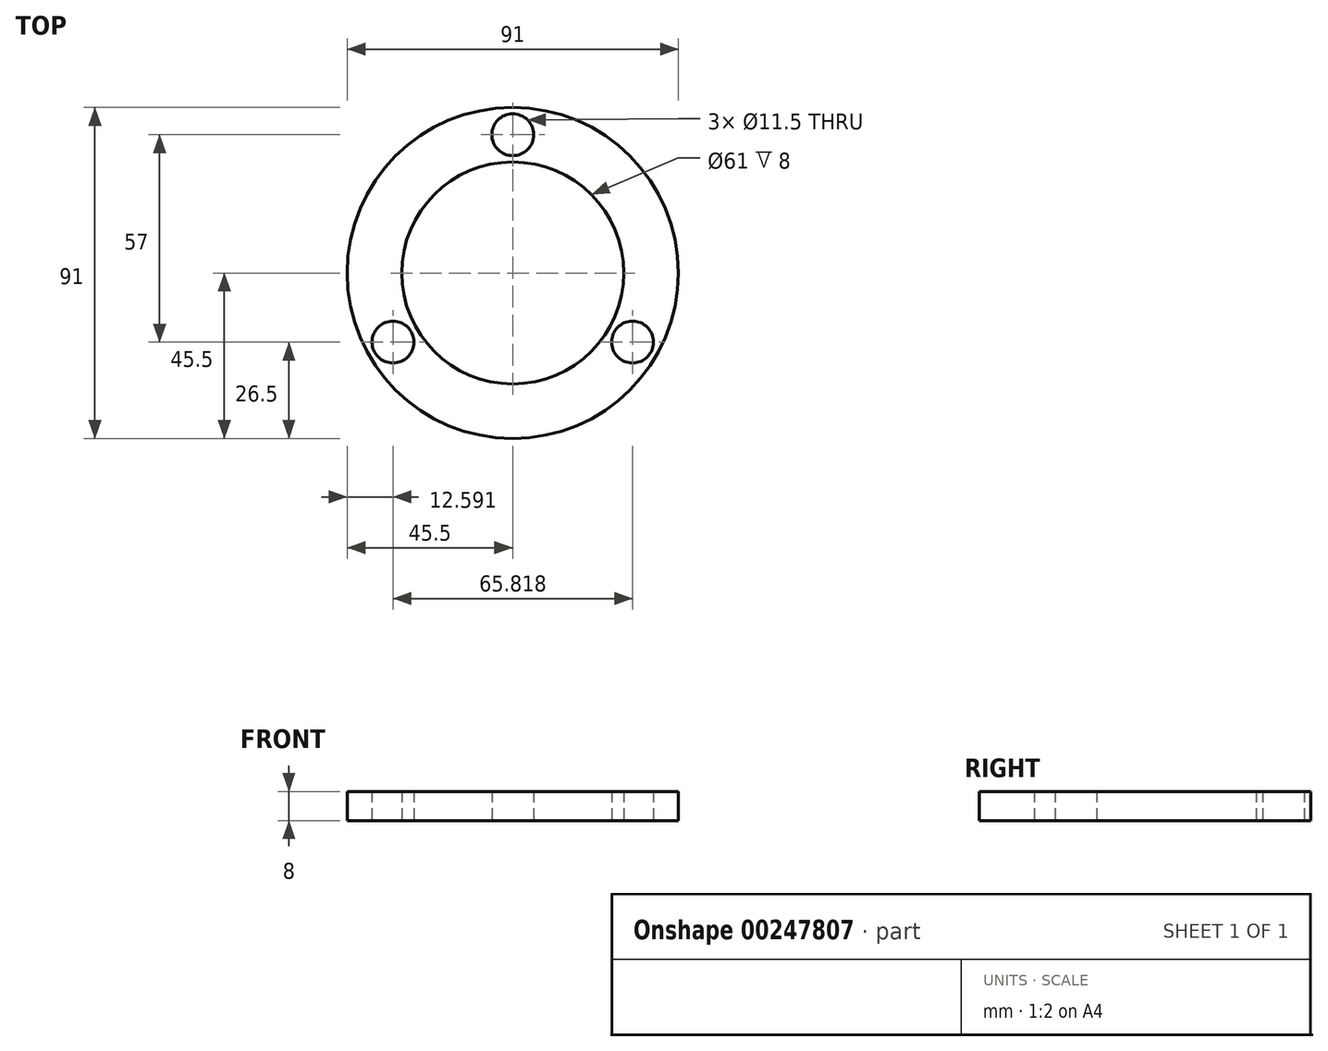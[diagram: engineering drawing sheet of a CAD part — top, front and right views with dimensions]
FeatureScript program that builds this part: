
annotation { "Feature Type Name" : "Feature", "Feature Type Description" : "" }
export const myFeature = defineFeature(function(context is Context, id is Id, definition is map)
    precondition{}
    {
        {
            var Q0;
            Q0=qCreatedBy(makeId("Top.planeOp"),FACE);
            var sketch = newSketch(context, id + "F0", { "sketchPlane" : qUnion([Q0])});
            skCircle(sketch, "E0", {"center": v(0, 0) * mm, "radius": 38 * mm});
            skCircle(sketch, "E1", {"center": v(0, 0) * mm, "radius": 45.5 * mm});
            skCircle(sketch, "E2", {"center": v(0, 0) * mm, "radius": 30.5 * mm});
            skCircle(sketch, "E3.cCircle", {"center": v(0, 0) * mm, "radius": 38 * mm, "construction": true});
            skLineSegment(sketch, "E3.0", {"start": v(0, 38) * mm, "end": v(32.9, -19) * mm});
            skLineSegment(sketch, "E3.1", {"start": v(32.9, -19) * mm, "end": v(-32.9, -19) * mm});
            skLineSegment(sketch, "E3.2", {"start": v(-32.9, -19) * mm, "end": v(0, 38) * mm});
            skCircle(sketch, "E4", {"center": v(0, 38) * mm, "radius": 5.75 * mm});
            skCircle(sketch, "E5", {"center": v(32.9, -19) * mm, "radius": 5.75 * mm});
            skCircle(sketch, "E6", {"center": v(-32.9, -19) * mm, "radius": 5.75 * mm});
            skSolve(sketch);
        }
        {
            var Q0;
            Q0 = qSketchRegion(id + "F0", true);
            var Q1;
            Q1=makeQuery(id+"F0.imprint","IMPRINT",FACE,{"disambiguationData":[TD([[makeQuery(id+"F0.imprint","IMPRINT",EDGE,{"derivedFrom":sQuery(id+"F0.wireOp",EDGE,"E2")}),-1.0]])]});
            var Q2;
            {var subQ3=sQuery(id+"F0.wireOp",EDGE,"E4");var subQ5=sQuery(id+"F0.wireOp",EDGE,"E0");var subQ6=makeQuery(id+"F0.imprint","INTERSECT",VERTEX,{"disambiguationData":[OD(1.0)],"derivedFrom":[subQ5,subQ3]});Q2=makeQuery(id+"F0.imprint","IMPRINT",FACE,{"disambiguationData":[TD([[makeQuery(id+"F0.imprint","IMPRINT",EDGE,{"disambiguationData":[TD([[subQ6,-1.0]])],"derivedFrom":subQ5}),1.0]])]});}
            var Q3;
            {var subQ3=sQuery(id+"F0.wireOp",EDGE,"E6");var subQ7=sQuery(id+"F0.wireOp",EDGE,"E0");var subQ10=makeQuery(id+"F0.imprint","INTERSECT",VERTEX,{"disambiguationData":[OD(1.0)],"derivedFrom":[subQ7,subQ3]});Q3=makeQuery(id+"F0.imprint","IMPRINT",FACE,{"disambiguationData":[TD([[makeQuery(id+"F0.imprint","IMPRINT",EDGE,{"disambiguationData":[TD([[subQ10,-1.0]])],"derivedFrom":subQ7}),1.0]])]});}
            var Q4;
            {var subQ6=sQuery(id+"F0.wireOp",EDGE,"E4");var subQ8=sQuery(id+"F0.wireOp",EDGE,"E0");var subQ9=makeQuery(id+"F0.imprint","INTERSECT",VERTEX,{"disambiguationData":[OD(0.0)],"derivedFrom":[subQ8,subQ6]});Q4=makeQuery(id+"F0.imprint","IMPRINT",FACE,{"disambiguationData":[TD([[makeQuery(id+"F0.imprint","IMPRINT",EDGE,{"disambiguationData":[TD([[subQ9,1.0]])],"derivedFrom":subQ8}),1.0]])]});}
            extrude(context, id + "F1", {"entities" : qUnion([Q0, Q1, Q2, Q3, Q4]), "depth" : 8 * mm});
        }
    });
